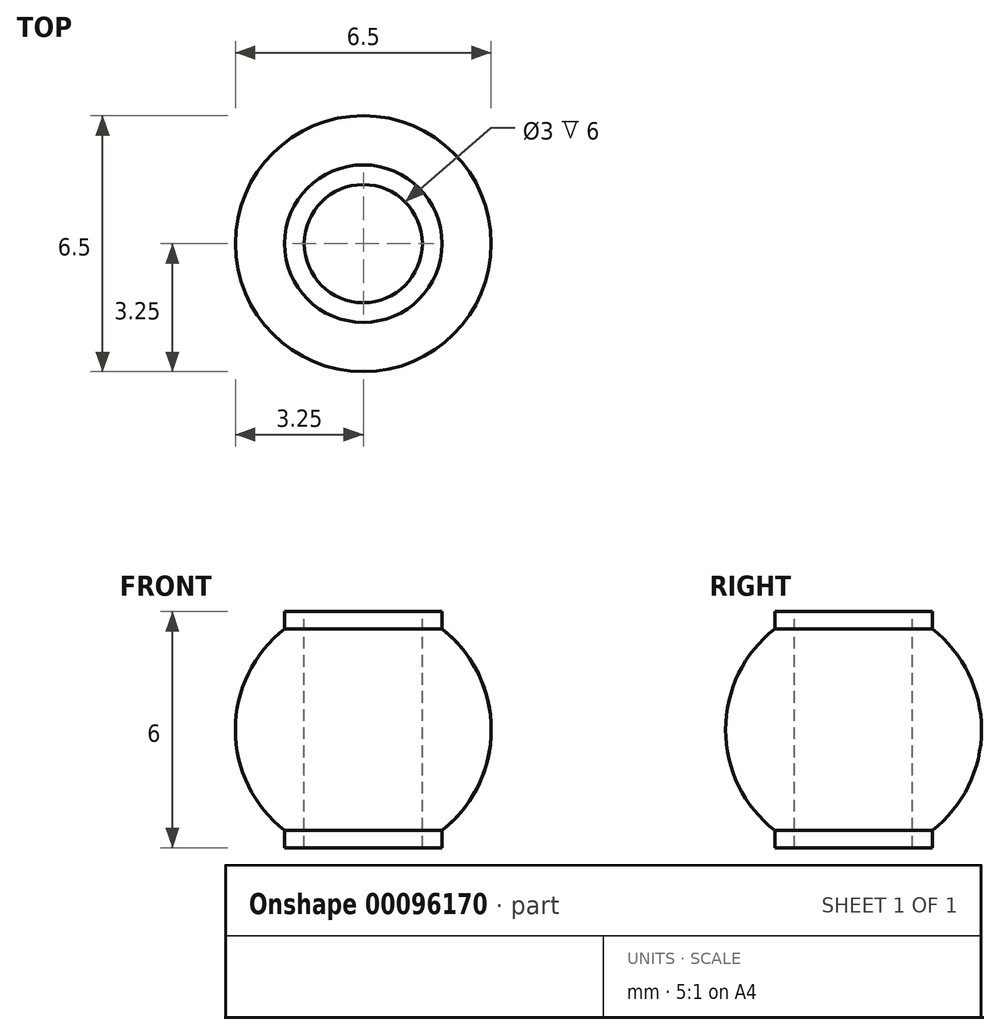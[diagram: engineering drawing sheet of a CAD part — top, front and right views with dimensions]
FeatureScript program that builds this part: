
annotation { "Feature Type Name" : "Feature", "Feature Type Description" : "" }
export const myFeature = defineFeature(function(context is Context, id is Id, definition is map)
    precondition{}
    {
        {
            var Q0;
            Q0=qCreatedBy(makeId("Right.planeOp"),FACE);
            var sketch = newSketch(context, id + "F0", { "sketchPlane" : qUnion([Q0])});
            skArc(sketch, "E0", {"start": v(2, -2.56) * mm, "mid": v(3.25, 0) * mm, "end": v(2, 2.56) * mm});
            skLineSegment(sketch, "E1", {"start": v(0, 3.25) * mm, "end": v(0, -3.25) * mm, "construction": true});
            skLineSegment(sketch, "E2", {"start": v(1.5, 3) * mm, "end": v(1.5, -3) * mm});
            skLineSegment(sketch, "E3", {"start": v(1.5, -3) * mm, "end": v(2, -3) * mm});
            skLineSegment(sketch, "E4", {"start": v(2, -3) * mm, "end": v(2, -2.56) * mm});
            skLineSegment(sketch, "E5", {"start": v(2, 3) * mm, "end": v(1.5, 3) * mm});
            skLineSegment(sketch, "E6.trimOffspring", {"start": v(2, 2.56) * mm, "end": v(2, 3) * mm});
            skSolve(sketch);
        }
        {
            var Q0;
            Q0 = qSketchRegion(id + "F0", true);
            var Q1;
            Q1=sQuery(id+"F0.wireOp",EDGE,"E1");
            revolve(context, id + "F1", {"entities" : qUnion([Q0]), "axis" : qUnion([Q1]), "revolveType" : RevolveType.FULL});
        }
    });
